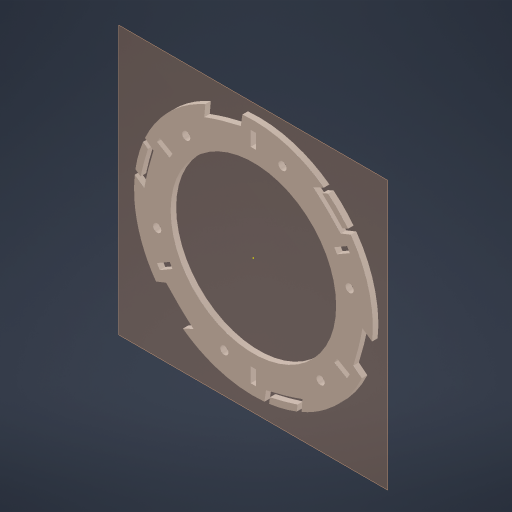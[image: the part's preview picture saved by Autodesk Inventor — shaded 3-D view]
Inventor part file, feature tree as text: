
AUTODESK INVENTOR PART (.ipt)
format: ipt  version: 2023 (Build 270158000, 158)  size: 406,528 bytes
history: native  units: mm
features: reference x17, other x11, sketch x6, extrude x5, pattern_circular x3, plane x1, projected_geometry x1
ambient origin geometry x8: Origin, YZ Plane, XZ Plane, XY Plane, X Axis, Y Axis, Z Axis, Center Point
bodies: Solid1 (feature_tree)
feature tree (44):
  plane  "Work Plane1"
  extrude  "Extrusion1"  Depth=3.0mm TaperAngle=0.0deg
  sketch  "Sketch2"  dims[d3=1.5mm d4=3.0mm d5=0.0mm d6=30.0mm d7=360.0deg]
  extrude  "Extrusion2"  Depth=3.0mm TaperAngle=0.0deg
  pattern_circular  "Circular Pattern1"  Count=3 Angle=360.0deg
  extrude  "Extrusion3"  Depth=10.0mm
  extrude  "Extrusion4"  Depth=10.0mm TaperAngle=360.0deg
  pattern_circular  "Circular Pattern2"  Count=6 Angle=360.0deg
  extrude  "Extrusion5"  [1 undecoded]
  pattern_circular  "Circular Pattern3"  [2 undecoded]
  sketch  "Sketch1"  dims[d0=90.0mm d1=3.0mm d2=0.0mm]
  reference  "Reference1"
  reference  "Reference2"
  reference  "Reference3"
  reference  "Reference4"
  reference  "Reference5"
  reference  "Reference6"
  reference  "Reference7"
  reference  "Reference8"
  reference  "Reference9"
  reference  "Reference10"
  reference  "Reference11"
  reference  "Reference12"
  reference  "Reference13"
  sketch  "Sketch3"  dims[d9=10.0mm d10=0.0mm d11=4.5mm]
  reference  "Reference14"
  sketch  "Sketch4"  dims[d12=10.0mm d13=0.0mm d14=60.0mm d15=360.0deg]
  reference  "Reference15"
  reference  "Reference16"
  projected_geometry  "Projected Loop1"
  reference  "Reference17"
  sketch  "Sketch5"  dims[d17=10.0mm d18=0.0mm d19=60.0mm d20=360.0deg]
  sketch  "Sketch6"
  parser-record x1  (decoder bookkeeping rows leaked as tree rows — omitted from the tree; the rows remain in map.json)
  other  "assembly.iam"
  other  "vase:1"
  other  "SpantB:3"
  other  "SpantB:2"
  other  "SpantB:1"
  other  "SpantA:2"
  other  "SpantA:3"
  other  "SpantA:1"
  other  "Assembly1"
  other  "vase_v2._tom:1"
note: 3 required parameter values undecoded (feature->parameter linkage not recoverable at this tier; creation-order binding heuristic only, values carry confidence <= 0.55)
note: 1 file-system path scrubbed to <path> (originals preserved in map.json)
